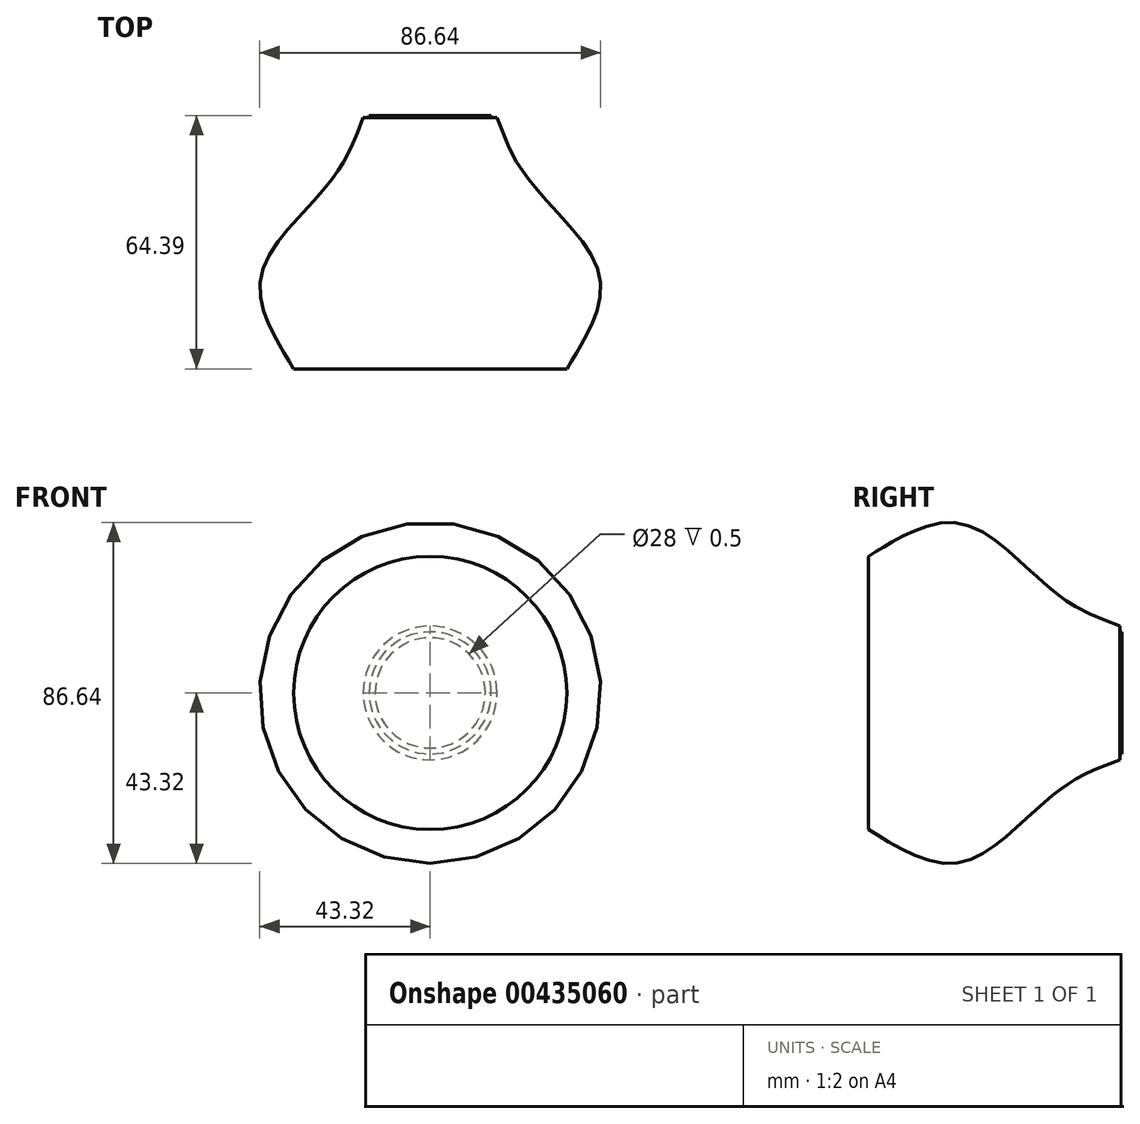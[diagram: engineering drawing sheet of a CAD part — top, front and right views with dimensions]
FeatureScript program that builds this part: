
annotation { "Feature Type Name" : "Feature", "Feature Type Description" : "" }
export const myFeature = defineFeature(function(context is Context, id is Id, definition is map)
    precondition{}
    {
        {
            var Q0;
            Q0=qCreatedBy(makeId("Front.planeOp"),FACE);
            var sketch = newSketch(context, id + "F0", { "sketchPlane" : qUnion([Q0])});
            skCircle(sketch, "E0", {"center": v(0, 0) * mm, "radius": 14 * mm});
            skLineSegment(sketch, "E1", {"start": v(-14, 0) * mm, "end": v(14, 0) * mm, "construction": true});
            skCircle(sketch, "E2", {"center": v(0, 0) * mm, "radius": 15.5 * mm});
            skCircle(sketch, "E3", {"center": v(9, 0) * mm, "radius": 2 * mm});
            skCircle(sketch, "E4", {"center": v(-9, 0) * mm, "radius": 2 * mm});
            skCircle(sketch, "E5", {"center": v(4.68, 11.31) * mm, "radius": 1.68 * mm});
            skCircle(sketch, "E6", {"center": v(-5.8, -10.54) * mm, "radius": 1.84 * mm});
            skSolve(sketch);
        }
        {
            var Q0;
            Q0=qSketchRegion(id+"F0",true);
            extrude(context, id + "F1", {"entities" : qUnion([Q0]), "depth" : 28 * mm});
        }
        {
            var Q0;
            Q0=makeQuery(id+"F0.imprint","IMPRINT",FACE,{"disambiguationData":[TD([[makeQuery(id+"F0.imprint","IMPRINT",EDGE,{"derivedFrom":sQuery(id+"F0.wireOp",EDGE,"E0")}),1.0]])]});
            extrude(context, id + "F2", {"entities" : qUnion([Q0]), "operationType" : NewBodyOperationType.ADD, "depth" : 3 * mm});
        }
        {
            var Q0;
            Q0=qCreatedBy(makeId("Top.planeOp"),FACE);
            var sketch = newSketch(context, id + "F3", { "sketchPlane" : qUnion([Q0])});
            skLineSegment(sketch, "E7", {"start": v(0, -28) * mm, "end": v(-17, -28) * mm});
            skFitSpline(sketch, "E8", {"points": [v(-17, -28) * mm, v(-23.37, -41.48) * mm, v(-32.67, -52.53) * mm, v(-43.32, -71.4) * mm, v(-34.7, -91.89) * mm], "startDerivative": vector(-34.48, -91.7) * mm, "endDerivative": vector(27, -46.5) * mm});
            skLineSegment(sketch, "E9", {"start": v(-34.7, -91.89) * mm, "end": v(0, -91.89) * mm});
            skLineSegment(sketch, "E10", {"start": v(0, -91.89) * mm, "end": v(0, -28) * mm});
            skSolve(sketch);
        }
        {
            var Q0;
            Q0=makeQuery(id+"F3.imprint","IMPRINT",FACE,{"disambiguationData":[TD([[makeQuery(id+"F3.imprint","IMPRINT",EDGE,{"derivedFrom":sQuery(id+"F3.wireOp",EDGE,"E7")}),1.0]])]});
            var Q1;
            Q1=sQuery(id+"F3.wireOp",EDGE,"E10");
            revolve(context, id + "F4", {"entities" : qUnion([Q0]), "axis" : qUnion([Q1]), "revolveType" : RevolveType.FULL});
        }
        {
            var Q0;
            Q0=qCreatedBy(makeId("Right.planeOp"),FACE);
            var sketch = newSketch(context, id + "F5", { "sketchPlane" : qUnion([Q0])});
            skLineSegment(sketch, "E11.bottom", {"start": v(0, 41.9) * mm, "end": v(-27.5, 41.9) * mm});
            skLineSegment(sketch, "E11.top", {"start": v(0, -42.28) * mm, "end": v(-27.5, -42.28) * mm});
            skLineSegment(sketch, "E11.left", {"start": v(0, 41.9) * mm, "end": v(0, -42.28) * mm});
            skLineSegment(sketch, "E11.right", {"start": v(-27.5, 41.9) * mm, "end": v(-27.5, -42.28) * mm});
            skSolve(sketch);
        }
        {
            var Q0;
            Q0=makeQuery(id+"F5.imprint","IMPRINT",FACE,{"disambiguationData":[TD([[makeQuery(id+"F5.imprint","IMPRINT",EDGE,{"derivedFrom":sQuery(id+"F5.wireOp",EDGE,"E11.bottom")}),1.0]])]});
            extrude(context, id + "F6", {"entities" : qUnion([Q0]), "operationType" : NewBodyOperationType.REMOVE, "endBound" : BoundingType.SYMMETRIC, "oppositeDirection" : true, "depth" : 999 * mm});
        }
    });
